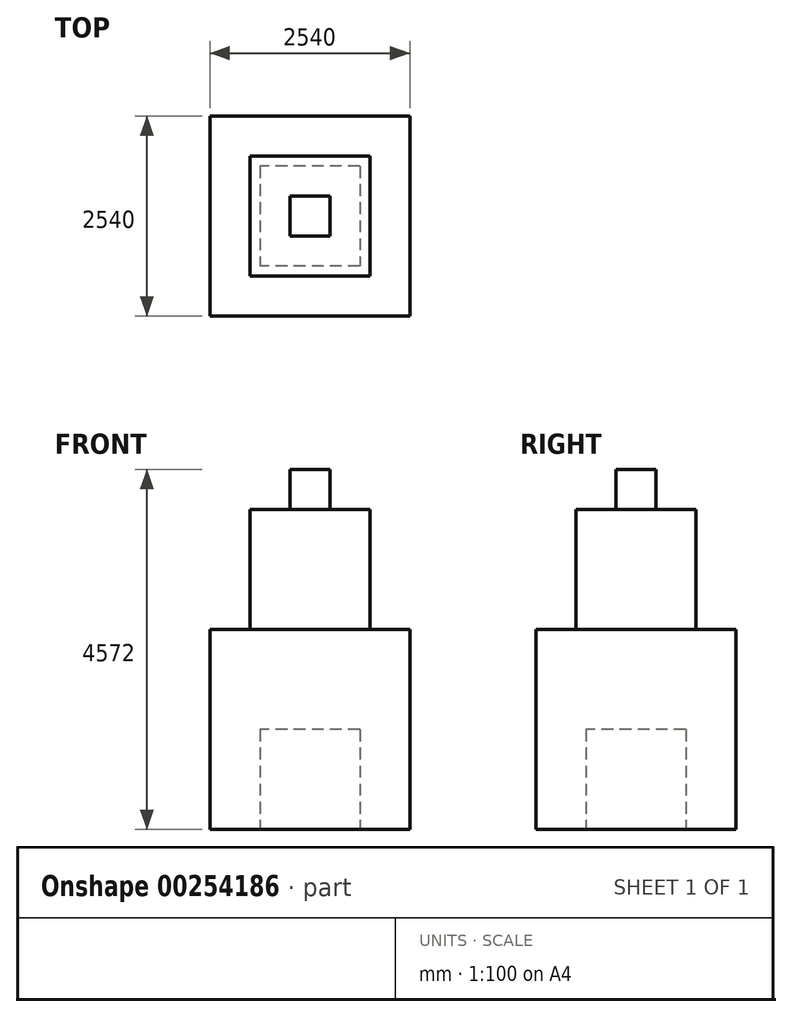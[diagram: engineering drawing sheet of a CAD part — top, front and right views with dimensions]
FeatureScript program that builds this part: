
annotation { "Feature Type Name" : "Feature", "Feature Type Description" : "" }
export const myFeature = defineFeature(function(context is Context, id is Id, definition is map)
    precondition{}
    {
        {
            var Q0;
            Q0=qCreatedBy(makeId("Top.planeOp"),FACE);
            var sketch = newSketch(context, id + "F0", { "sketchPlane" : qUnion([Q0])});
            skLineSegment(sketch, "E0.bottom", {"start": v(-1270, 1270) * mm, "end": v(1270, 1270) * mm});
            skLineSegment(sketch, "E0.top", {"start": v(-1270, -1270) * mm, "end": v(1270, -1270) * mm});
            skLineSegment(sketch, "E0.left", {"start": v(-1270, 1270) * mm, "end": v(-1270, -1270) * mm});
            skLineSegment(sketch, "E0.right", {"start": v(1270, 1270) * mm, "end": v(1270, -1270) * mm});
            skSolve(sketch);
        }
        {
            var Q0;
            Q0=makeQuery(id+"F0.imprint","IMPRINT",FACE,{"disambiguationData":[TD([[makeQuery(id+"F0.imprint","IMPRINT",EDGE,{"derivedFrom":sQuery(id+"F0.wireOp",EDGE,"E0.bottom")}),-1.0]])]});
            extrude(context, id + "F1", {"entities" : qUnion([Q0]), "depth" : 2540 * mm});
        }
        {
            var Q0;
            Q0=makeQuery(id+"F1.opExtrude","CAP_FACE",FACE,{"disambiguationData":[OSD([sQuery(id+"F0.wireOp",EDGE,"E0.bottom"),sQuery(id+"F0.wireOp",EDGE,"E0.top"),sQuery(id+"F0.wireOp",EDGE,"E0.left"),sQuery(id+"F0.wireOp",EDGE,"E0.right")])],"isStart":false});
            var sketch = newSketch(context, id + "F2", { "sketchPlane" : qUnion([Q0])});
            skLineSegment(sketch, "E1.bottom", {"start": v(-762, 762) * mm, "end": v(762, 762) * mm});
            skLineSegment(sketch, "E1.top", {"start": v(-762, -762) * mm, "end": v(762, -762) * mm});
            skLineSegment(sketch, "E1.left", {"start": v(-762, 762) * mm, "end": v(-762, -762) * mm});
            skLineSegment(sketch, "E1.right", {"start": v(762, 762) * mm, "end": v(762, -762) * mm});
            skSolve(sketch);
        }
        {
            var Q0;
            Q0=makeQuery(id+"F2.imprint","IMPRINT",FACE,{"disambiguationData":[TD([[makeQuery(id+"F2.imprint","IMPRINT",EDGE,{"derivedFrom":sQuery(id+"F2.wireOp",EDGE,"E1.bottom")}),-1.0]])]});
            extrude(context, id + "F3", {"entities" : qUnion([Q0]), "operationType" : NewBodyOperationType.ADD, "depth" : 1524 * mm});
        }
        {
            var Q0;
            Q0=makeQuery(id+"F3.opExtrude","CAP_FACE",FACE,{"disambiguationData":[OSD([sQuery(id+"F2.wireOp",EDGE,"E1.bottom"),sQuery(id+"F2.wireOp",EDGE,"E1.top"),sQuery(id+"F2.wireOp",EDGE,"E1.left"),sQuery(id+"F2.wireOp",EDGE,"E1.right")])],"isStart":false});
            var sketch = newSketch(context, id + "F4", { "sketchPlane" : qUnion([Q0])});
            skLineSegment(sketch, "E2.bottom", {"start": v(-254, -254) * mm, "end": v(254, -254) * mm});
            skLineSegment(sketch, "E2.top", {"start": v(-254, 254) * mm, "end": v(254, 254) * mm});
            skLineSegment(sketch, "E2.left", {"start": v(-254, -254) * mm, "end": v(-254, 254) * mm});
            skLineSegment(sketch, "E2.right", {"start": v(254, -254) * mm, "end": v(254, 254) * mm});
            skSolve(sketch);
        }
        {
            var Q0;
            Q0=makeQuery(id+"F4.imprint","IMPRINT",FACE,{"disambiguationData":[TD([[makeQuery(id+"F4.imprint","IMPRINT",EDGE,{"derivedFrom":sQuery(id+"F4.wireOp",EDGE,"E2.bottom")}),1.0]])]});
            extrude(context, id + "F5", {"entities" : qUnion([Q0]), "operationType" : NewBodyOperationType.ADD, "depth" : 508 * mm});
        }
        {
            var Q0;
            Q0=makeQuery(id+"F1.opExtrude","CAP_FACE",FACE,{"disambiguationData":[OSD([sQuery(id+"F0.wireOp",EDGE,"E0.bottom"),sQuery(id+"F0.wireOp",EDGE,"E0.top"),sQuery(id+"F0.wireOp",EDGE,"E0.left"),sQuery(id+"F0.wireOp",EDGE,"E0.right")])],"isStart":true});
            var sketch = newSketch(context, id + "F6", { "sketchPlane" : qUnion([Q0])});
            skLineSegment(sketch, "E3.bottom", {"start": v(635, -635) * mm, "end": v(-635, -635) * mm});
            skLineSegment(sketch, "E3.top", {"start": v(635, 635) * mm, "end": v(-635, 635) * mm});
            skLineSegment(sketch, "E3.left", {"start": v(635, -635) * mm, "end": v(635, 635) * mm});
            skLineSegment(sketch, "E3.right", {"start": v(-635, -635) * mm, "end": v(-635, 635) * mm});
            skSolve(sketch);
        }
        {
            var Q0;
            Q0=makeQuery(id+"F6.imprint","IMPRINT",FACE,{"disambiguationData":[TD([[makeQuery(id+"F6.imprint","IMPRINT",EDGE,{"derivedFrom":sQuery(id+"F6.wireOp",EDGE,"E3.bottom")}),-1.0]])]});
            extrude(context, id + "F7", {"entities" : qUnion([Q0]), "operationType" : NewBodyOperationType.REMOVE, "oppositeDirection" : true, "depth" : 1270 * mm});
        }
    });
